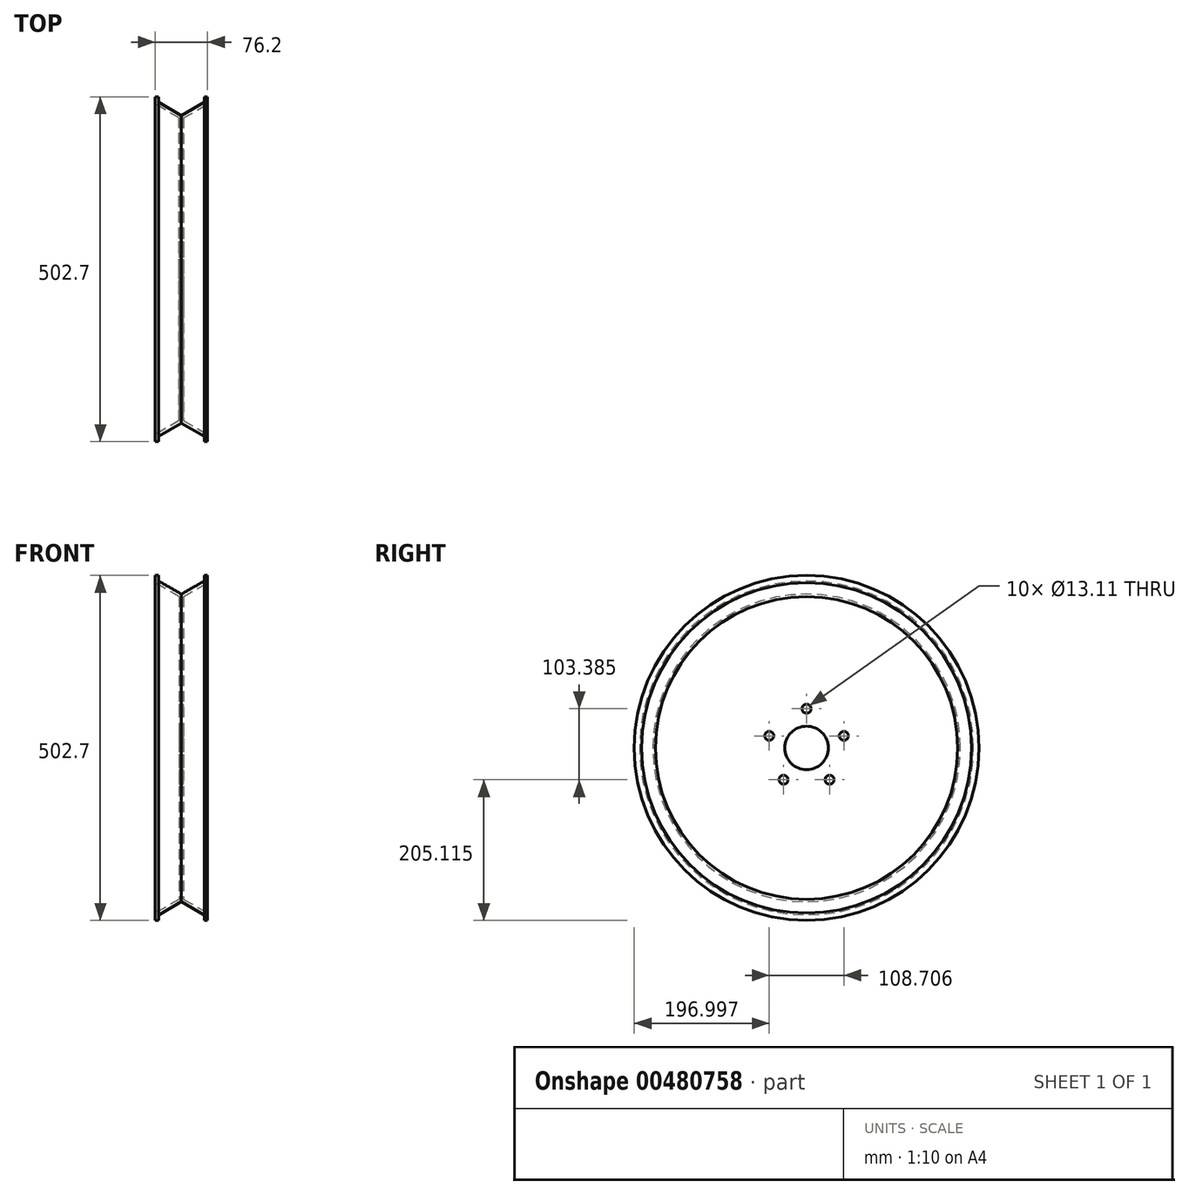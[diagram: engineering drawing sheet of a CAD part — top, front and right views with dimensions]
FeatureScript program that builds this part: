
annotation { "Feature Type Name" : "Feature", "Feature Type Description" : "" }
export const myFeature = defineFeature(function(context is Context, id is Id, definition is map)
    precondition{}
    {
        {
            var Q0;
            Q0=qCreatedBy(makeId("Front.planeOp"),FACE);
            var sketch = newSketch(context, id + "F0", { "sketchPlane" : qUnion([Q0])});
            skLineSegment(sketch, "E0", {"start": v(-3.18, 31.75) * mm, "end": v(-3.18, 220.5) * mm});
            skLineSegment(sketch, "E1", {"start": v(-3.18, 220.5) * mm, "end": v(-38.1, 240.66) * mm});
            skLineSegment(sketch, "E2", {"start": v(-38.1, 240.66) * mm, "end": v(-38.1, 251.35) * mm});
            skLineSegment(sketch, "E3", {"start": v(-38.1, 251.35) * mm, "end": v(-33.34, 251.35) * mm});
            skLineSegment(sketch, "E4", {"start": v(-33.34, 251.35) * mm, "end": v(-33.34, 243.41) * mm});
            skLineSegment(sketch, "E5", {"start": v(-33.34, 243.41) * mm, "end": v(0, 224.16) * mm});
            skLineSegment(sketch, "E6", {"start": v(3.18, 220.5) * mm, "end": v(3.18, 31.75) * mm});
            skLineSegment(sketch, "E7", {"start": v(3.17, 31.75) * mm, "end": v(-3.17, 31.75) * mm});
            skLineSegment(sketch, "E8", {"start": v(0, 31.75) * mm, "end": v(0, 233.16) * mm, "construction": true});
            skLineSegment(sketch, "E9.MirrorCS", {"start": v(3.18, 220.5) * mm, "end": v(38.1, 240.66) * mm});
            skLineSegment(sketch, "E10.MirrorCS", {"start": v(38.1, 240.66) * mm, "end": v(38.1, 251.35) * mm});
            skLineSegment(sketch, "E11.MirrorCS", {"start": v(33.34, 251.35) * mm, "end": v(33.34, 243.41) * mm});
            skLineSegment(sketch, "E12.MirrorCS", {"start": v(38.1, 251.35) * mm, "end": v(33.34, 251.35) * mm});
            skLineSegment(sketch, "E13", {"start": v(33.34, 243.41) * mm, "end": v(0, 224.16) * mm});
            skLineSegment(sketch, "E14", {"start": v(0, 0) * mm, "end": v(85.05, 0) * mm, "construction": true});
            skSolve(sketch);
        }
        {
            var Q0;
            Q0=qSketchRegion(id+"F0",true);
            var Q1;
            Q1=sQuery(id+"F0.wireOp",EDGE,"E14");
            revolve(context, id + "F1", {"entities" : qUnion([Q0]), "axis" : qUnion([Q1]), "revolveType" : RevolveType.FULL});
        }
        {
            var Q0;
            Q0=makeQuery(id+"F1.opRevolve","SWEPT_FACE",FACE,{"disambiguationData":[OSD([sQuery(id+"F0.wireOp",EDGE,"E6")])]});
            var sketch = newSketch(context, id + "F2", { "sketchPlane" : qUnion([Q0])});
            skPoint(sketch, "E15", {"position": v(0, 57.15) * mm});
            skCircle(sketch, "E16", {"center": v(0, 0) * mm, "radius": 57.15 * mm, "construction": true});
            skPoint(sketch, "E17.1.0", {"position": v(-54.35, 17.66) * mm});
            skPoint(sketch, "E17.2.0", {"position": v(-33.6, -46.24) * mm});
            skPoint(sketch, "E17.3.0", {"position": v(33.6, -46.24) * mm});
            skPoint(sketch, "E17.4.0", {"position": v(54.35, 17.66) * mm});
            skSolve(sketch);
        }
        {
            var Q0;
            Q0=sQuery(id+"F2.wireOp",VERTEX,"E15");
            var Q1;
            Q1=sQuery(id+"F2.wireOp",VERTEX,"E17.4.0");
            var Q2;
            Q2=sQuery(id+"F2.wireOp",VERTEX,"E17.3.0");
            var Q3;
            Q3=sQuery(id+"F2.wireOp",VERTEX,"E17.2.0");
            var Q4;
            Q4=sQuery(id+"F2.wireOp",VERTEX,"E17.1.0");
            var Q5;
            Q5=makeQuery(id+"F1.opRevolve","SWEPT_BODY",BODY,{"disambiguationData":[OSD([sQuery(id+"F0.wireOp",EDGE,"E0"),sQuery(id+"F0.wireOp",EDGE,"E1"),sQuery(id+"F0.wireOp",EDGE,"E2"),sQuery(id+"F0.wireOp",EDGE,"E3"),sQuery(id+"F0.wireOp",EDGE,"E4"),sQuery(id+"F0.wireOp",EDGE,"E5"),sQuery(id+"F0.wireOp",EDGE,"E6"),sQuery(id+"F0.wireOp",EDGE,"E7"),sQuery(id+"F0.wireOp",EDGE,"E9.MirrorCS"),sQuery(id+"F0.wireOp",EDGE,"E10.MirrorCS"),sQuery(id+"F0.wireOp",EDGE,"E11.MirrorCS"),sQuery(id+"F0.wireOp",EDGE,"E12.MirrorCS"),sQuery(id+"F0.wireOp",EDGE,"E13")])]});
            hole(context, id + "F3", {"style" : HoleStyle.SIMPLE, "endStyle" : HoleEndStyle.THROUGH, "standardTappedOrClearance" : lookupTablePath({ "standard" : "ANSI", "fit" : "Close", "size" : "1/2", "type" : "Clearance" }), "standardBlindInLast" : lookupTablePath({ "fit" : "Close", "standard" : "ANSI", "size" : "1/2", "type" : "Clearance" }), "holeDiameter" : 13.1 * mm, "isTappedThrough" : true, "tappedDepth" : 12.7 * mm, "tapClearance" : 3, "locations" : qUnion([Q0, Q1, Q2, Q3, Q4]), "scope" : qUnion([Q5])});
        }
    });
